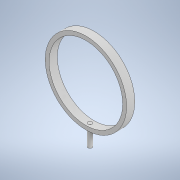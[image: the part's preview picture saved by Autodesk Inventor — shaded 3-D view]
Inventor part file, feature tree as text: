
AUTODESK INVENTOR PART (.ipt)
format: ipt  version: 2022 (Build 260153000, 153)  size: 133,120 bytes
history: native  units: in
note: dims shown in document units (in); Inventor stores cm internally (conversion verified against a paired STEP export)
features: sketch x5, extrude x4, revolve x1
ambient origin geometry x8: Origin, YZ Plane, XZ Plane, XY Plane, X Axis, Y Axis, Z Axis, Center Point
bodies: Solid1 (feature_tree)
feature tree (10):
  sketch  "Sketch1"  dims[d0=1.25in d2=90.0deg]
  sketch  "Sketch2"  dims[d3=0.25in d4=0.0in d5=2.25in]
  revolve  "Revolution1"  Angle=90.0deg
  extrude  "Extrusion1"  Depth=2.25in
  extrude  "Extrusion2"  Depth=0.125in
  extrude  "Extrusion3"  Depth=1.125in TaperAngle=0.0deg
  extrude  "Extrusion4"  [1 undecoded]
  sketch  "Sketch3"  dims[d6=0.25in d7=0.0in d8=0.125in]
  sketch  "Sketch5"  dims[d9=1.75in d10=0.0in d11=1.125in d12=0.0in]
  sketch  "Sketch6"
note: 1 required parameter value undecoded (feature->parameter linkage not recoverable at this tier; creation-order binding heuristic only, values carry confidence <= 0.55)
